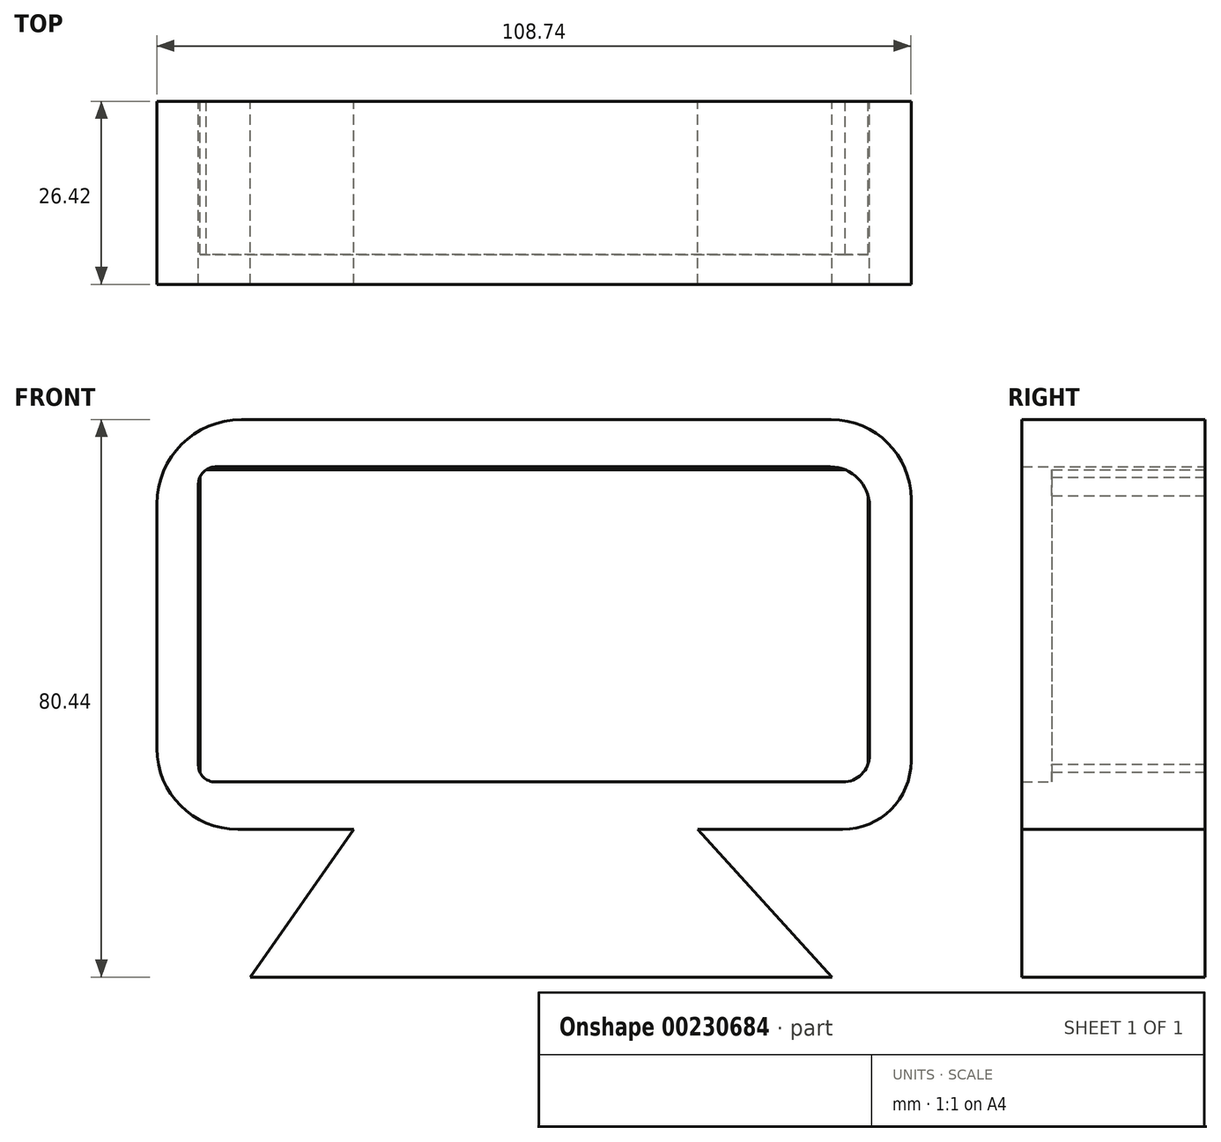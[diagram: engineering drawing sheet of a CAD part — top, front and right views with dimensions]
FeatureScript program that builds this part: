
annotation { "Feature Type Name" : "Feature", "Feature Type Description" : "" }
export const myFeature = defineFeature(function(context is Context, id is Id, definition is map)
    precondition{}
    {
        {
            var Q0;
            Q0=qCreatedBy(makeId("Front.planeOp"),FACE);
            var sketch = newSketch(context, id + "F0", { "sketchPlane" : qUnion([Q0])});
            skLineSegment(sketch, "E0.bottom", {"start": v(-42.2, 52.32) * mm, "end": v(42.88, 52.32) * mm});
            skLineSegment(sketch, "E0.top", {"start": v(-42.71, -6.81) * mm, "end": v(44.5, -6.81) * mm});
            skLineSegment(sketch, "E0.left", {"start": v(-54.37, 40.14) * mm, "end": v(-54.37, 4.85) * mm});
            skLineSegment(sketch, "E0.right", {"start": v(54.37, 40.82) * mm, "end": v(54.37, 3.05) * mm});
            skPoint(sketch, "E0.middle", {"position": v(0, 22.75) * mm});
            skLineSegment(sketch, "E1", {"start": v(-25.96, -6.81) * mm, "end": v(-40.94, -28.12) * mm});
            skLineSegment(sketch, "E2", {"start": v(-40.94, -28.12) * mm, "end": v(43, -28.12) * mm});
            skLineSegment(sketch, "E3", {"start": v(43, -28.12) * mm, "end": v(23.62, -6.81) * mm});
            skLineSegment(sketch, "E4.bottom", {"start": v(-45.9, 45.49) * mm, "end": v(42.72, 45.49) * mm});
            skLineSegment(sketch, "E4.top", {"start": v(-45.96, 0.02) * mm, "end": v(44.53, 0.02) * mm});
            skLineSegment(sketch, "E4.left", {"start": v(-48.38, 43.01) * mm, "end": v(-48.38, 2.43) * mm});
            skLineSegment(sketch, "E4.right", {"start": v(48.38, 39.83) * mm, "end": v(48.38, 3.86) * mm});
            skPoint(sketch, "E5.visualSharp", {"position": v(-54.37, 52.32) * mm});
            skArc(sketch, "E5.filletArc", {"start": v(-42.2, 52.32) * mm, "mid": v(-50.8, 48.75) * mm, "end": v(-54.37, 40.14) * mm});
            skPoint(sketch, "E6.visualSharp", {"position": v(54.37, 52.32) * mm});
            skArc(sketch, "E6.filletArc", {"start": v(54.37, 40.82) * mm, "mid": v(51, 48.95) * mm, "end": v(42.88, 52.32) * mm});
            skPoint(sketch, "E7.visualSharp", {"position": v(54.37, -6.81) * mm});
            skArc(sketch, "E7.filletArc", {"start": v(44.5, -6.81) * mm, "mid": v(51.48, -3.92) * mm, "end": v(54.37, 3.05) * mm});
            skPoint(sketch, "E8.visualSharp", {"position": v(-54.37, -6.81) * mm});
            skArc(sketch, "E8.filletArc", {"start": v(-54.37, 4.85) * mm, "mid": v(-50.96, -3.4) * mm, "end": v(-42.71, -6.81) * mm});
            skPoint(sketch, "E9.visualSharp", {"position": v(-48.38, 45.49) * mm});
            skArc(sketch, "E9.filletArc", {"start": v(-45.9, 45.49) * mm, "mid": v(-47.65, 44.76) * mm, "end": v(-48.38, 43.01) * mm});
            skPoint(sketch, "E10.visualSharp", {"position": v(-48.38, 0.02) * mm});
            skArc(sketch, "E10.filletArc", {"start": v(-48.38, 2.43) * mm, "mid": v(-47.67, 0.73) * mm, "end": v(-45.96, 0.02) * mm});
            skPoint(sketch, "E11.visualSharp", {"position": v(48.38, 45.49) * mm});
            skArc(sketch, "E11.filletArc", {"start": v(48.38, 39.83) * mm, "mid": v(46.72, 43.83) * mm, "end": v(42.72, 45.49) * mm});
            skPoint(sketch, "E12.visualSharp", {"position": v(48.38, 0.02) * mm});
            skArc(sketch, "E12.filletArc", {"start": v(44.53, 0.02) * mm, "mid": v(47.25, 1.14) * mm, "end": v(48.38, 3.86) * mm});
            skSolve(sketch);
        }
        {
            var Q0;
            Q0 = qSketchRegion(id + "F0", true);
            extrude(context, id + "F1", {"entities" : qUnion([Q0]), "depth" : 26.42 * mm});
        }
        {
            var Q0;
            Q0=qCreatedBy(makeId("Front.planeOp"),FACE);
            var sketch = newSketch(context, id + "F2", { "sketchPlane" : qUnion([Q0])});
            skLineSegment(sketch, "E13.bottom", {"start": v(48.17, 45.07) * mm, "end": v(-48.17, 45.07) * mm});
            skLineSegment(sketch, "E13.top", {"start": v(48.17, 0) * mm, "end": v(-48.17, 0) * mm});
            skLineSegment(sketch, "E13.left", {"start": v(48.17, 45.07) * mm, "end": v(48.17, 0) * mm});
            skLineSegment(sketch, "E13.right", {"start": v(-48.17, 45.07) * mm, "end": v(-48.17, 0) * mm});
            skPoint(sketch, "E13.middle", {"position": v(0, 22.54) * mm});
            skSolve(sketch);
        }
        {
            var Q0;
            Q0 = qSketchRegion(id + "F2", true);
            extrude(context, id + "F3", {"entities" : qUnion([Q0]), "operationType" : NewBodyOperationType.ADD, "depth" : 22.1 * mm});
        }
    });
